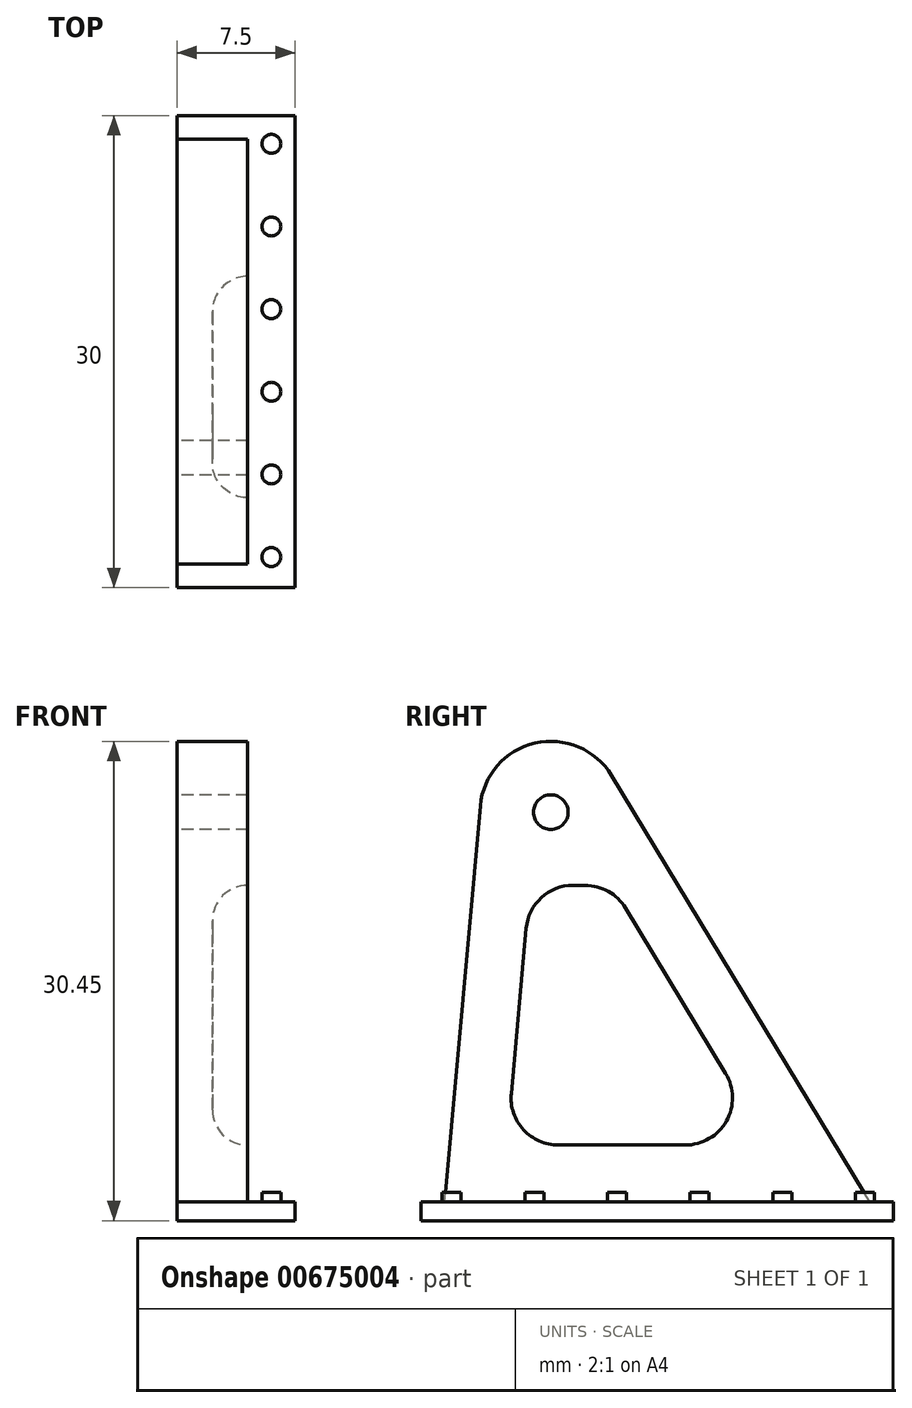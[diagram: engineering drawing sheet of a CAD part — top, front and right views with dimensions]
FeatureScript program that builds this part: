
annotation { "Feature Type Name" : "Feature", "Feature Type Description" : "" }
export const myFeature = defineFeature(function(context is Context, id is Id, definition is map)
    precondition{}
    {
        {
            assignVariable(context, id + "F0", {"name" : "Faktor", "anyValue" : 1.5});
        }
        {
            var Q0;
            Q0=qCreatedBy(makeId("Right.planeOp"),FACE);
            var sketch = newSketch(context, id + "F1", { "sketchPlane" : qUnion([Q0])});
            skLineSegment(sketch, "E0.bottom", {"start": v(-8.25, 0) * mm, "end": v(21.75, 0) * mm});
            skLineSegment(sketch, "E0.top", {"start": v(-8.25, 1.2) * mm, "end": v(21.75, 1.2) * mm});
            skLineSegment(sketch, "E0.left", {"start": v(-8.25, 0) * mm, "end": v(-8.25, 1.2) * mm});
            skLineSegment(sketch, "E0.right", {"start": v(21.75, 0) * mm, "end": v(21.75, 1.2) * mm});
            skSolve(sketch);
        }
        {
            var Q0;
            Q0=qSketchRegion(id+"F1",true);
            extrude(context, id + "F2", {"entities" : qUnion([Q0]), "depth" : getVariable(context, 'Faktor') * 5 * mm, "offsetDistance" : 25 * mm});
        }
        {
            var Q0;
            Q0=qCreatedBy(makeId("Right.planeOp"),FACE);
            var sketch = newSketch(context, id + "F3", { "sketchPlane" : qUnion([Q0])});
            skCircle(sketch, "E1", {"center": v(0, 25.95) * mm, "radius": 1.1 * mm});
            skLineSegment(sketch, "E2.0", {"start": v(-8.25, 1.2) * mm, "end": v(21.75, 1.2) * mm, "construction": true});
            skLineSegment(sketch, "E3", {"start": v(20.25, 1.2) * mm, "end": v(3.85, 28.28) * mm});
            skLineSegment(sketch, "E4", {"start": v(20.25, 1.2) * mm, "end": v(-6.75, 1.2) * mm});
            skLineSegment(sketch, "E5", {"start": v(-6.75, 1.2) * mm, "end": v(-4.48, 26.35) * mm});
            skArc(sketch, "E6", {"start": v(3.85, 28.28) * mm, "mid": v(-1.01, 30.33) * mm, "end": v(-4.48, 26.35) * mm});
            skSolve(sketch);
        }
        {
            var Q0;
            Q0=qSketchRegion(id+"F3",true);
            extrude(context, id + "F4", {"entities" : qUnion([Q0]), "operationType" : NewBodyOperationType.ADD, "depth" : getVariable(context, 'Faktor') * 3 * mm, "offsetDistance" : 25 * mm});
        }
        {
            var Q0;
            Q0=makeQuery(id+"F4.opExtrude","CAP_FACE",FACE,{"disambiguationData":[OSD([sQuery(id+"F3.wireOp",EDGE,"E1"),sQuery(id+"F3.wireOp",EDGE,"E3"),sQuery(id+"F3.wireOp",EDGE,"E4"),sQuery(id+"F3.wireOp",EDGE,"E5"),sQuery(id+"F3.wireOp",EDGE,"E6")])],"isStart":false});
            var sketch = newSketch(context, id + "F5", { "sketchPlane" : qUnion([Q0])});
            skLineSegment(sketch, "E7", {"start": v(-2.81, 4.8) * mm, "end": v(13.86, 4.8) * mm});
            skLineSegment(sketch, "E8", {"start": v(13.86, 4.8) * mm, "end": v(3.87, 21.3) * mm});
            skLineSegment(sketch, "E9", {"start": v(3.87, 21.3) * mm, "end": v(-1.32, 21.3) * mm});
            skLineSegment(sketch, "E10", {"start": v(-1.32, 21.3) * mm, "end": v(-2.81, 4.8) * mm});
            skSolve(sketch);
        }
        {
            var Q0;
            Q0=qSketchRegion(id+"F5",true);
            extrude(context, id + "F6", {"entities" : qUnion([Q0]), "operationType" : NewBodyOperationType.REMOVE, "oppositeDirection" : true, "depth" : getVariable(context, 'Faktor') * 1.5 * mm, "offsetDistance" : 25 * mm});
        }
        {
            var Q0;
            Q0=makeQuery(id+"F6.boolean.opBoolean","COPY",EDGE,{"derivedFrom":makeQuery(id+"F6.opExtrude","SWEPT_EDGE",EDGE,{"disambiguationData":[OSD([sQuery(id+"F5.wireOp",EDGE,"E9"),sQuery(id+"F5.wireOp",EDGE,"E10")])]})});
            var Q1;
            Q1=makeQuery(id+"F6.boolean.opBoolean","COPY",EDGE,{"derivedFrom":makeQuery(id+"F6.opExtrude","SWEPT_EDGE",EDGE,{"disambiguationData":[OSD([sQuery(id+"F5.wireOp",EDGE,"E8"),sQuery(id+"F5.wireOp",EDGE,"E9")])]})});
            var Q2;
            Q2=makeQuery(id+"F6.boolean.opBoolean","COPY",EDGE,{"derivedFrom":makeQuery(id+"F6.opExtrude","SWEPT_EDGE",EDGE,{"disambiguationData":[OSD([sQuery(id+"F5.wireOp",EDGE,"E7"),sQuery(id+"F5.wireOp",EDGE,"E8")])]})});
            var Q3;
            Q3=makeQuery(id+"F6.boolean.opBoolean","COPY",EDGE,{"derivedFrom":makeQuery(id+"F6.opExtrude","SWEPT_EDGE",EDGE,{"disambiguationData":[OSD([sQuery(id+"F5.wireOp",EDGE,"E7"),sQuery(id+"F5.wireOp",EDGE,"E10")])]})});
            fillet(context, id + "F7", {"entities" : qUnion([Q0, Q1, Q2, Q3]), "radius" : getVariable(context, 'Faktor') * 2 * mm, "tangentPropagation" : true, "allowEdgeOverflow" : false});
        }
        {
            var Q0;
            Q0=makeQuery(id+"F6.boolean.opBoolean","COPY",FACE,{"derivedFrom":makeQuery(id+"F6.opExtrude","CAP_FACE",FACE,{"disambiguationData":[OSD([sQuery(id+"F5.wireOp",EDGE,"E7"),sQuery(id+"F5.wireOp",EDGE,"E8"),sQuery(id+"F5.wireOp",EDGE,"E9"),sQuery(id+"F5.wireOp",EDGE,"E10")])],"isStart":false})});
            fillet(context, id + "F8", {"entities" : qUnion([Q0]), "radius" : getVariable(context, 'Faktor') * 1.5 * mm, "tangentPropagation" : true, "allowEdgeOverflow" : false});
        }
        {
            var Q0;
            Q0=makeQuery(id+"F2.opExtrude","SWEPT_FACE",FACE,{"disambiguationData":[OSD([sQuery(id+"F1.wireOp",EDGE,"E0.top")])]});
            var sketch = newSketch(context, id + "F9", { "sketchPlane" : qUnion([Q0])});
            skLineSegment(sketch, "E11", {"start": v(6, 21.8) * mm, "end": v(6, 0.99) * mm, "construction": true});
            skCircle(sketch, "E12", {"center": v(6, 19.95) * mm, "radius": 0.6 * mm});
            skCircle(sketch, "E13.1.0.0", {"center": v(6, 14.7) * mm, "radius": 0.6 * mm});
            skCircle(sketch, "E13.2.0.0", {"center": v(6, 9.45) * mm, "radius": 0.6 * mm});
            skCircle(sketch, "E13.3.0.0", {"center": v(6, 4.2) * mm, "radius": 0.6 * mm});
            skCircle(sketch, "E13.4.0.0", {"center": v(6, -1.05) * mm, "radius": 0.6 * mm});
            skCircle(sketch, "E13.5.0.0", {"center": v(6, -6.3) * mm, "radius": 0.6 * mm});
            skLineSegment(sketch, "E13.direction1", {"start": v(6, 19.95) * mm, "end": v(6, 14.7) * mm, "construction": true});
            skSolve(sketch);
        }
        {
            var Q0;
            Q0=qSketchRegion(id+"F9",true);
            extrude(context, id + "F10", {"entities" : qUnion([Q0]), "operationType" : NewBodyOperationType.ADD, "depth" : getVariable(context, 'Faktor') * 0.4 * mm, "offsetDistance" : 25 * mm});
        }
    });
